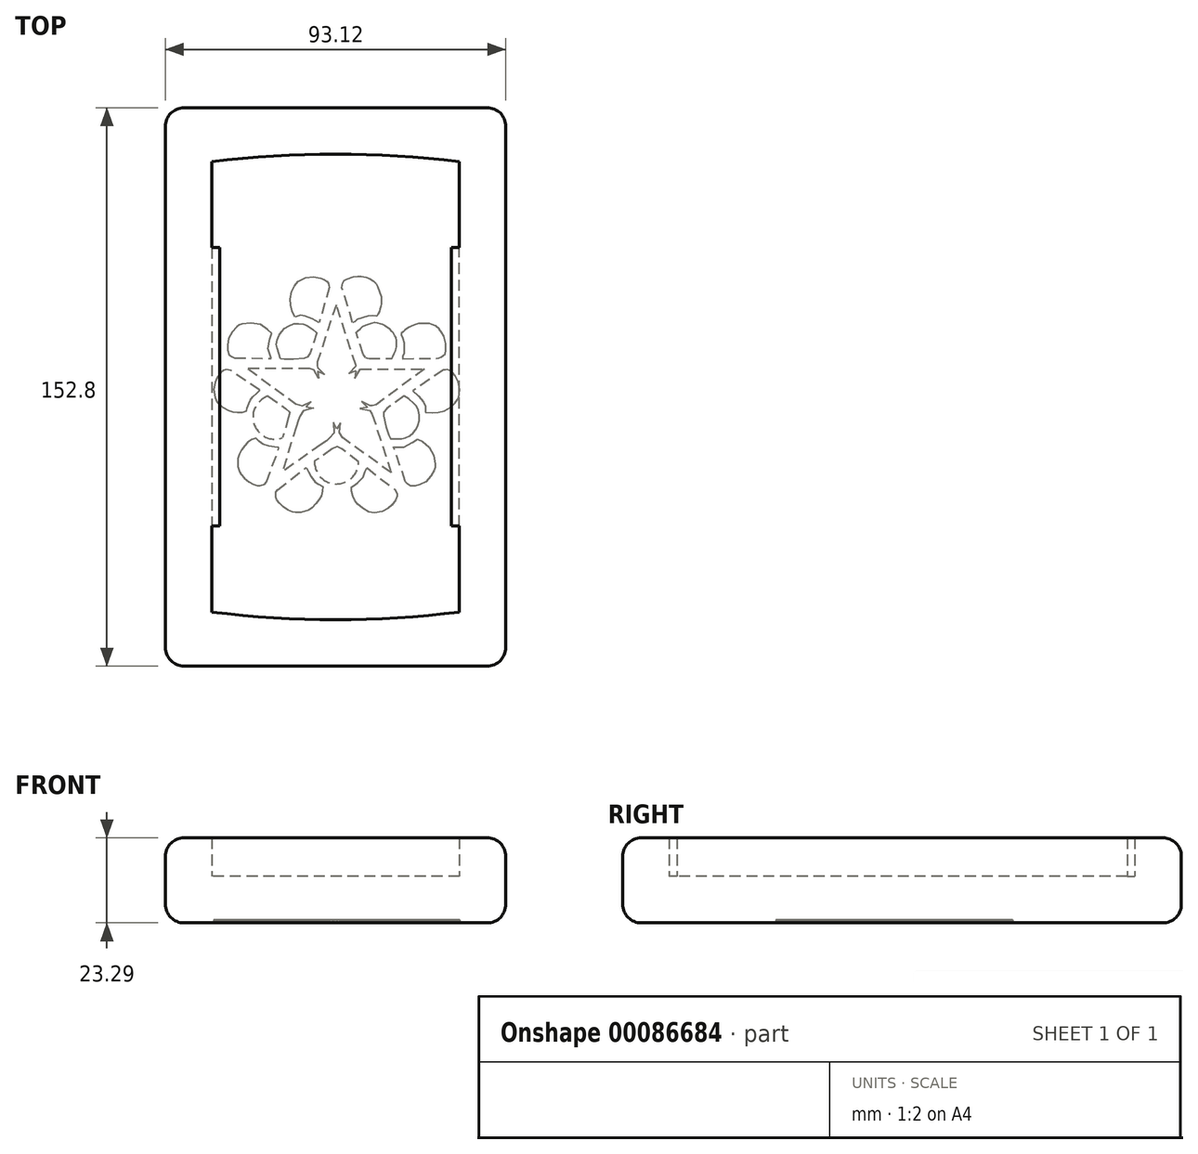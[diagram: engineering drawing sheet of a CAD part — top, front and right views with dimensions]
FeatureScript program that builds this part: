
annotation { "Feature Type Name" : "Feature", "Feature Type Description" : "" }
export const myFeature = defineFeature(function(context is Context, id is Id, definition is map)
    precondition{}
    {
        {
            var Q0;
            Q0=qCreatedBy(makeId("Top.planeOp"),FACE);
            var sketch = newSketch(context, id + "F0", { "sketchPlane" : qUnion([Q0])});
            skLineSegment(sketch, "E0.left", {"start": v(33.86, 61.62) * mm, "end": v(33.86, -61.62) * mm});
            skLineSegment(sketch, "E0.right", {"start": v(-33.86, 61.62) * mm, "end": v(-33.86, -61.62) * mm});
            skPoint(sketch, "E0.middle", {"position": v(0, 0) * mm});
            skLineSegment(sketch, "E1.bottom", {"start": v(0, 63.7) * mm, "end": v(0, 63.7) * mm});
            skLineSegment(sketch, "E1.top", {"start": v(0, -63.7) * mm, "end": v(0, -63.7) * mm});
            skArc(sketch, "E2", {"start": v(33.86, 61.62) * mm, "mid": v(0, 63.7) * mm, "end": v(-33.86, 61.62) * mm});
            skArc(sketch, "E3", {"start": v(-33.86, -61.62) * mm, "mid": v(0, -63.7) * mm, "end": v(33.86, -61.62) * mm});
            skLineSegment(sketch, "E4.bottom", {"start": v(46.56, 76.4) * mm, "end": v(-46.56, 76.4) * mm});
            skLineSegment(sketch, "E4.top", {"start": v(46.56, -76.4) * mm, "end": v(-46.56, -76.4) * mm});
            skLineSegment(sketch, "E4.left", {"start": v(46.56, 76.4) * mm, "end": v(46.56, -76.4) * mm});
            skLineSegment(sketch, "E4.right", {"start": v(-46.56, 76.4) * mm, "end": v(-46.56, -76.4) * mm});
            skSolve(sketch);
        }
        {
            var Q0;
            Q0=makeQuery(id+"F0.imprint","IMPRINT",FACE,{"disambiguationData":[TD([[makeQuery(id+"F0.imprint","IMPRINT",EDGE,{"derivedFrom":sQuery(id+"F0.wireOp",EDGE,"E0.left")}),-1.0]])]});
            extrude(context, id + "F1", {"entities" : qUnion([Q0]), "depth" : 12.7 * mm});
        }
        {
            var Q0;
            Q0=makeQuery(id+"F0.imprint","IMPRINT",FACE,{"disambiguationData":[TD([[makeQuery(id+"F0.imprint","IMPRINT",EDGE,{"derivedFrom":sQuery(id+"F0.wireOp",EDGE,"E0.left")}),1.0]])]});
            extrude(context, id + "F2", {"entities" : qUnion([Q0]), "operationType" : NewBodyOperationType.ADD, "depth" : 23.3 * mm});
        }
        {
            var Q0;
            Q0=makeQuery(id+"F2.opExtrude","SWEPT_FACE",FACE,{"disambiguationData":[OSD([sQuery(id+"F0.wireOp",EDGE,"E4.bottom")])]});
            var Q1;
            Q1=makeQuery(id+"F2.opExtrude","SWEPT_FACE",FACE,{"disambiguationData":[OSD([sQuery(id+"F0.wireOp",EDGE,"E4.left")])]});
            var Q2;
            Q2=makeQuery(id+"F2.opExtrude","SWEPT_FACE",FACE,{"disambiguationData":[OSD([sQuery(id+"F0.wireOp",EDGE,"E4.right")])]});
            var Q3;
            {var subQ0=sQuery(id+"F0.wireOp",EDGE,"E3");var subQ1=sQuery(id+"F0.wireOp",EDGE,"E2");var subQ2=sQuery(id+"F0.wireOp",EDGE,"E0.right");var subQ3=sQuery(id+"F0.wireOp",EDGE,"E0.left");Q3=makeQuery(id+"F2.boolean.opBoolean","MERGE",FACE,{"derivedFrom":[makeQuery(id+"F1.opExtrude","CAP_FACE",FACE,{"disambiguationData":[OSD([subQ3,subQ2,subQ1,subQ0])],"isStart":true}),makeQuery(id+"F2.opExtrude","CAP_FACE",FACE,{"disambiguationData":[OSD([subQ3,subQ2,subQ1,subQ0,sQuery(id+"F0.wireOp",EDGE,"E4.bottom"),sQuery(id+"F0.wireOp",EDGE,"E4.top"),sQuery(id+"F0.wireOp",EDGE,"E4.left"),sQuery(id+"F0.wireOp",EDGE,"E4.right")])],"isStart":true})]});}
            var Q4;
            Q4=makeQuery(id+"F2.opExtrude","SWEPT_FACE",FACE,{"disambiguationData":[OSD([sQuery(id+"F0.wireOp",EDGE,"E4.top")])]});
            fillet(context, id + "F3", {"entities" : qUnion([Q0, Q1, Q2, Q3, Q4]), "radius" : 5.08 * mm, "tangentPropagation" : true, "allowEdgeOverflow" : false});
        }
        {
            var Q0;
            Q0=makeQuery(id+"F2.opExtrude","SWEPT_FACE",FACE,{"disambiguationData":[OSD([sQuery(id+"F0.wireOp",EDGE,"E0.right")])]});
            var sketch = newSketch(context, id + "F4", { "sketchPlane" : qUnion([Q0])});
            skLineSegment(sketch, "E5.bottom", {"start": v(38.13, 23.3) * mm, "end": v(-38.07, 23.3) * mm});
            skLineSegment(sketch, "E5.top", {"start": v(38.13, 23.24) * mm, "end": v(-38.07, 23.24) * mm});
            skLineSegment(sketch, "E5.left", {"start": v(38.13, 23.3) * mm, "end": v(38.13, 23.24) * mm});
            skLineSegment(sketch, "E5.right", {"start": v(-38.07, 23.3) * mm, "end": v(-38.07, 23.24) * mm});
            skPoint(sketch, "E5.middle", {"position": v(0.03, 23.27) * mm});
            skSolve(sketch);
        }
        {
            var Q0;
            Q0=qSketchRegion(id+"F4",true);
            extrude(context, id + "F5", {"entities" : qUnion([Q0]), "operationType" : NewBodyOperationType.ADD, "depth" : 2.16 * mm});
        }
        {
            var Q0;
            Q0=makeQuery(id+"F2.opExtrude","SWEPT_FACE",FACE,{"disambiguationData":[OSD([sQuery(id+"F0.wireOp",EDGE,"E0.left")])]});
            var sketch = newSketch(context, id + "F6", { "sketchPlane" : qUnion([Q0])});
            skLineSegment(sketch, "E6.bottom", {"start": v(38.1, 23.3) * mm, "end": v(-38.1, 23.3) * mm});
            skLineSegment(sketch, "E6.top", {"start": v(38.1, 23.24) * mm, "end": v(-38.1, 23.24) * mm});
            skLineSegment(sketch, "E6.left", {"start": v(38.1, 23.3) * mm, "end": v(38.1, 23.24) * mm});
            skLineSegment(sketch, "E6.right", {"start": v(-38.1, 23.3) * mm, "end": v(-38.1, 23.24) * mm});
            skPoint(sketch, "E6.middle", {"position": v(0, 23.27) * mm});
            skSolve(sketch);
        }
        {
            var Q0;
            Q0=qSketchRegion(id+"F6",true);
            extrude(context, id + "F7", {"entities" : qUnion([Q0]), "operationType" : NewBodyOperationType.ADD, "depth" : 2.16 * mm});
        }
        {
            var Q0;
            {var subQ0=sQuery(id+"F0.wireOp",EDGE,"E3");var subQ1=sQuery(id+"F0.wireOp",EDGE,"E2");var subQ2=sQuery(id+"F0.wireOp",EDGE,"E0.right");var subQ3=sQuery(id+"F0.wireOp",EDGE,"E0.left");Q0=makeQuery(id+"F2.boolean.opBoolean","MERGE",FACE,{"derivedFrom":[makeQuery(id+"F1.opExtrude","CAP_FACE",FACE,{"disambiguationData":[OSD([subQ3,subQ2,subQ1,subQ0])],"isStart":true}),makeQuery(id+"F2.opExtrude","CAP_FACE",FACE,{"disambiguationData":[OSD([subQ3,subQ2,subQ1,subQ0,sQuery(id+"F0.wireOp",EDGE,"E4.bottom"),sQuery(id+"F0.wireOp",EDGE,"E4.top"),sQuery(id+"F0.wireOp",EDGE,"E4.left"),sQuery(id+"F0.wireOp",EDGE,"E4.right")])],"isStart":true})]});}
            var sketch = newSketch(context, id + "F8", { "sketchPlane" : qUnion([Q0])});
            skLineSegment(sketch, "E7", {"start": v(-21.27, 32.47) * mm, "end": v(-19.6, 31.78) * mm});
            skLineSegment(sketch, "E8", {"start": v(-19.6, 31.78) * mm, "end": v(-18.58, 31.78) * mm});
            skLineSegment(sketch, "E9", {"start": v(-18.58, 31.78) * mm, "end": v(-17.8, 32.76) * mm});
            skLineSegment(sketch, "E10", {"start": v(-17.8, 32.76) * mm, "end": v(-16.99, 33.84) * mm});
            skLineSegment(sketch, "E11", {"start": v(-16.99, 33.84) * mm, "end": v(-16.21, 34.55) * mm});
            skLineSegment(sketch, "E12", {"start": v(-16.21, 34.55) * mm, "end": v(-15.34, 35.36) * mm});
            skLineSegment(sketch, "E13", {"start": v(-15.34, 35.36) * mm, "end": v(-14.11, 36.07) * mm});
            skLineSegment(sketch, "E14", {"start": v(-14.11, 36.07) * mm, "end": v(-12.56, 36.76) * mm});
            skLineSegment(sketch, "E15", {"start": v(-12.56, 36.76) * mm, "end": v(-11.36, 37.15) * mm});
            skLineSegment(sketch, "E16", {"start": v(-11.36, 37.15) * mm, "end": v(-9.48, 37.15) * mm});
            skLineSegment(sketch, "E17", {"start": v(-9.48, 37.15) * mm, "end": v(-8.4, 36.84) * mm});
            skLineSegment(sketch, "E18", {"start": v(-8.4, 36.84) * mm, "end": v(-7.27, 36.3) * mm});
            skLineSegment(sketch, "E19", {"start": v(-7.27, 36.3) * mm, "end": v(-6.34, 35.7) * mm});
            skLineSegment(sketch, "E20", {"start": v(-6.34, 35.7) * mm, "end": v(-4.82, 34.45) * mm});
            skLineSegment(sketch, "E21", {"start": v(-4.82, 34.45) * mm, "end": v(-3.62, 32.98) * mm});
            skLineSegment(sketch, "E22", {"start": v(-3.62, 32.98) * mm, "end": v(-2.88, 31.54) * mm});
            skLineSegment(sketch, "E23", {"start": v(-2.88, 31.54) * mm, "end": v(-2.28, 29.72) * mm});
            skLineSegment(sketch, "E24", {"start": v(-2.28, 29.72) * mm, "end": v(-2.28, 27.54) * mm});
            skLineSegment(sketch, "E25", {"start": v(-2.28, 27.54) * mm, "end": v(2.77, 27.54) * mm});
            skLineSegment(sketch, "E26", {"start": v(2.77, 27.54) * mm, "end": v(2.77, 29.5) * mm});
            skLineSegment(sketch, "E27", {"start": v(2.77, 29.5) * mm, "end": v(2.88, 29.93) * mm});
            skLineSegment(sketch, "E28", {"start": v(2.88, 29.93) * mm, "end": v(3.16, 30.76) * mm});
            skLineSegment(sketch, "E29", {"start": v(3.16, 30.76) * mm, "end": v(3.54, 31.68) * mm});
            skLineSegment(sketch, "E30", {"start": v(3.54, 31.68) * mm, "end": v(3.9, 32.4) * mm});
            skLineSegment(sketch, "E31", {"start": v(3.9, 32.4) * mm, "end": v(4.44, 33.35) * mm});
            skLineSegment(sketch, "E32", {"start": v(4.44, 33.35) * mm, "end": v(5.66, 34.63) * mm});
            skLineSegment(sketch, "E33", {"start": v(5.66, 34.63) * mm, "end": v(7.02, 35.77) * mm});
            skLineSegment(sketch, "E34", {"start": v(7.02, 35.77) * mm, "end": v(8.66, 36.66) * mm});
            skLineSegment(sketch, "E35", {"start": v(8.66, 36.66) * mm, "end": v(10.1, 37.1) * mm});
            skLineSegment(sketch, "E36", {"start": v(10.1, 37.1) * mm, "end": v(11.8, 37.1) * mm});
            skLineSegment(sketch, "E37", {"start": v(11.8, 37.1) * mm, "end": v(12.73, 36.86) * mm});
            skLineSegment(sketch, "E38", {"start": v(12.73, 36.86) * mm, "end": v(14.16, 36.29) * mm});
            skLineSegment(sketch, "E39", {"start": v(14.16, 36.29) * mm, "end": v(15.13, 35.65) * mm});
            skLineSegment(sketch, "E40", {"start": v(15.13, 35.65) * mm, "end": v(16.14, 34.96) * mm});
            skLineSegment(sketch, "E41", {"start": v(16.14, 34.96) * mm, "end": v(17.24, 33.94) * mm});
            skLineSegment(sketch, "E42", {"start": v(17.24, 33.94) * mm, "end": v(18.1, 32.91) * mm});
            skLineSegment(sketch, "E43", {"start": v(18.1, 32.91) * mm, "end": v(18.87, 31.85) * mm});
            skLineSegment(sketch, "E44", {"start": v(18.87, 31.85) * mm, "end": v(19.38, 31.75) * mm});
            skLineSegment(sketch, "E45", {"start": v(19.38, 31.75) * mm, "end": v(19.9, 31.75) * mm});
            skLineSegment(sketch, "E46", {"start": v(19.9, 31.75) * mm, "end": v(20.48, 32.02) * mm});
            skLineSegment(sketch, "E47", {"start": v(20.48, 32.02) * mm, "end": v(21.15, 32.36) * mm});
            skLineSegment(sketch, "E48", {"start": v(21.15, 32.36) * mm, "end": v(21.48, 32.58) * mm});
            skLineSegment(sketch, "E49", {"start": v(21.48, 32.58) * mm, "end": v(21.48, 30.67) * mm});
            skLineSegment(sketch, "E50", {"start": v(21.48, 30.67) * mm, "end": v(21.48, 30.13) * mm});
            skLineSegment(sketch, "E51", {"start": v(21.48, 30.13) * mm, "end": v(21.75, 29.84) * mm});
            skLineSegment(sketch, "E52", {"start": v(21.75, 29.84) * mm, "end": v(21.91, 29.68) * mm});
            skLineSegment(sketch, "E53", {"start": v(21.91, 29.68) * mm, "end": v(22.88, 29.46) * mm});
            skLineSegment(sketch, "E54", {"start": v(22.88, 29.46) * mm, "end": v(24.3, 28.9) * mm});
            skLineSegment(sketch, "E55", {"start": v(24.3, 28.9) * mm, "end": v(25.68, 28.18) * mm});
            skLineSegment(sketch, "E56", {"start": v(25.68, 28.18) * mm, "end": v(26.6, 27.51) * mm});
            skLineSegment(sketch, "E57", {"start": v(26.6, 27.51) * mm, "end": v(27.55, 26.7) * mm});
            skLineSegment(sketch, "E58", {"start": v(27.55, 26.7) * mm, "end": v(28.24, 25.94) * mm});
            skLineSegment(sketch, "E59", {"start": v(28.24, 25.94) * mm, "end": v(28.75, 25.15) * mm});
            skLineSegment(sketch, "E60", {"start": v(28.75, 25.15) * mm, "end": v(29.25, 24.25) * mm});
            skLineSegment(sketch, "E61", {"start": v(29.25, 24.25) * mm, "end": v(29.62, 22.94) * mm});
            skLineSegment(sketch, "E62", {"start": v(29.62, 22.94) * mm, "end": v(29.62, 21.2) * mm});
            skLineSegment(sketch, "E63", {"start": v(29.62, 21.2) * mm, "end": v(29.47, 19.95) * mm});
            skLineSegment(sketch, "E64", {"start": v(29.47, 19.95) * mm, "end": v(29.11, 18.99) * mm});
            skLineSegment(sketch, "E65", {"start": v(29.11, 18.99) * mm, "end": v(28.56, 17.78) * mm});
            skLineSegment(sketch, "E66", {"start": v(28.56, 17.78) * mm, "end": v(27.74, 16.5) * mm});
            skLineSegment(sketch, "E67", {"start": v(27.74, 16.5) * mm, "end": v(27.09, 15.68) * mm});
            skLineSegment(sketch, "E68", {"start": v(27.09, 15.68) * mm, "end": v(26.37, 15.01) * mm});
            skLineSegment(sketch, "E69", {"start": v(26.37, 15.01) * mm, "end": v(25.39, 14.3) * mm});
            skLineSegment(sketch, "E70", {"start": v(25.39, 14.3) * mm, "end": v(24.12, 13.62) * mm});
            skLineSegment(sketch, "E71", {"start": v(24.12, 13.62) * mm, "end": v(23.25, 13.32) * mm});
            skLineSegment(sketch, "E72", {"start": v(23.25, 13.32) * mm, "end": v(22.98, 13.32) * mm});
            skLineSegment(sketch, "E73", {"start": v(22.98, 13.32) * mm, "end": v(22.98, 12.9) * mm});
            skLineSegment(sketch, "E74", {"start": v(22.98, 12.9) * mm, "end": v(23.57, 11.63) * mm});
            skLineSegment(sketch, "E75", {"start": v(23.57, 11.63) * mm, "end": v(24.07, 9.99) * mm});
            skLineSegment(sketch, "E76", {"start": v(24.07, 9.99) * mm, "end": v(24.55, 8.24) * mm});
            skLineSegment(sketch, "E77", {"start": v(24.55, 8.24) * mm, "end": v(25.04, 8.37) * mm});
            skLineSegment(sketch, "E78", {"start": v(25.04, 8.37) * mm, "end": v(26.4, 8.69) * mm});
            skLineSegment(sketch, "E79", {"start": v(26.4, 8.69) * mm, "end": v(27.63, 8.69) * mm});
            skLineSegment(sketch, "E80", {"start": v(27.63, 8.69) * mm, "end": v(28.99, 8.69) * mm});
            skLineSegment(sketch, "E81", {"start": v(28.99, 8.69) * mm, "end": v(30.34, 8.43) * mm});
            skLineSegment(sketch, "E82", {"start": v(30.34, 8.43) * mm, "end": v(31.78, 7.84) * mm});
            skLineSegment(sketch, "E83", {"start": v(31.78, 7.84) * mm, "end": v(33.1, 7.17) * mm});
            skLineSegment(sketch, "E84", {"start": v(33.1, 7.17) * mm, "end": v(34.13, 6.34) * mm});
            skLineSegment(sketch, "E85", {"start": v(34.13, 6.34) * mm, "end": v(35, 5.42) * mm});
            skLineSegment(sketch, "E86", {"start": v(35, 5.42) * mm, "end": v(35.78, 4.35) * mm});
            skLineSegment(sketch, "E87", {"start": v(35.78, 4.35) * mm, "end": v(36.28, 3.1) * mm});
            skLineSegment(sketch, "E88", {"start": v(36.28, 3.1) * mm, "end": v(36.41, 2.52) * mm});
            skLineSegment(sketch, "E89", {"start": v(36.41, 2.52) * mm, "end": v(36.41, 0.78) * mm});
            skLineSegment(sketch, "E90", {"start": v(36.41, 0.78) * mm, "end": v(36.41, -0.54) * mm});
            skLineSegment(sketch, "E91", {"start": v(36.41, -0.54) * mm, "end": v(35.56, -2.8) * mm});
            skLineSegment(sketch, "E92", {"start": v(35.56, -2.8) * mm, "end": v(35.05, -3.72) * mm});
            skLineSegment(sketch, "E93", {"start": v(35.05, -3.72) * mm, "end": v(34.58, -4.42) * mm});
            skLineSegment(sketch, "E94", {"start": v(34.58, -4.42) * mm, "end": v(33.74, -5.62) * mm});
            skLineSegment(sketch, "E95", {"start": v(33.74, -5.62) * mm, "end": v(33.74, -6.53) * mm});
            skLineSegment(sketch, "E96", {"start": v(33.74, -6.53) * mm, "end": v(34.2, -7.05) * mm});
            skLineSegment(sketch, "E97", {"start": v(34.2, -7.05) * mm, "end": v(35.23, -8.06) * mm});
            skLineSegment(sketch, "E98", {"start": v(35.23, -8.06) * mm, "end": v(34.19, -8.26) * mm});
            skLineSegment(sketch, "E99", {"start": v(34.19, -8.26) * mm, "end": v(33.47, -8.46) * mm});
            skLineSegment(sketch, "E100", {"start": v(33.47, -8.46) * mm, "end": v(32.65, -9.1) * mm});
            skLineSegment(sketch, "E101", {"start": v(32.65, -9.1) * mm, "end": v(32.65, -11.82) * mm});
            skLineSegment(sketch, "E102", {"start": v(32.65, -11.82) * mm, "end": v(32.24, -13.93) * mm});
            skLineSegment(sketch, "E103", {"start": v(32.24, -13.93) * mm, "end": v(31.52, -15.69) * mm});
            skLineSegment(sketch, "E104", {"start": v(31.52, -15.69) * mm, "end": v(30.52, -17.17) * mm});
            skLineSegment(sketch, "E105", {"start": v(30.52, -17.17) * mm, "end": v(29.45, -18.31) * mm});
            skLineSegment(sketch, "E106", {"start": v(29.45, -18.31) * mm, "end": v(27.46, -19.28) * mm});
            skLineSegment(sketch, "E107", {"start": v(27.46, -19.28) * mm, "end": v(25.53, -19.59) * mm});
            skLineSegment(sketch, "E108", {"start": v(25.53, -19.59) * mm, "end": v(24.13, -19.59) * mm});
            skLineSegment(sketch, "E109", {"start": v(24.13, -19.59) * mm, "end": v(23.04, -19.38) * mm});
            skLineSegment(sketch, "E110", {"start": v(23.04, -19.38) * mm, "end": v(21.7, -19.04) * mm});
            skLineSegment(sketch, "E111", {"start": v(21.7, -19.04) * mm, "end": v(20.63, -18.54) * mm});
            skLineSegment(sketch, "E112", {"start": v(20.63, -18.54) * mm, "end": v(19.62, -18.02) * mm});
            skLineSegment(sketch, "E113", {"start": v(19.62, -18.02) * mm, "end": v(18.92, -17.41) * mm});
            skLineSegment(sketch, "E114", {"start": v(18.92, -17.41) * mm, "end": v(18.3, -16.85) * mm});
            skLineSegment(sketch, "E115", {"start": v(18.3, -16.85) * mm, "end": v(17.6, -16.01) * mm});
            skLineSegment(sketch, "E116", {"start": v(17.6, -16.01) * mm, "end": v(17.18, -15.46) * mm});
            skLineSegment(sketch, "E117", {"start": v(17.18, -15.46) * mm, "end": v(14.88, -17.16) * mm});
            skLineSegment(sketch, "E118.MirrorCS", {"start": v(-11.14, -31.34) * mm, "end": v(-10.64, -31.65) * mm});
            skLineSegment(sketch, "E119.MirrorCS", {"start": v(-16.35, -15.66) * mm, "end": v(-15.33, -16.61) * mm});
            skLineSegment(sketch, "E120.MirrorCS", {"start": v(-34.29, -7.9) * mm, "end": v(-34.6, -8.14) * mm});
            skLineSegment(sketch, "E121.MirrorCS", {"start": v(-10.64, -31.65) * mm, "end": v(-8.98, -32.19) * mm});
            skLineSegment(sketch, "E122.MirrorCS", {"start": v(-12.2, -30.48) * mm, "end": v(-11.14, -31.34) * mm});
            skLineSegment(sketch, "E123.MirrorCS", {"start": v(-17.4, -16.52) * mm, "end": v(-16.84, -15.79) * mm});
            skLineSegment(sketch, "E124.MirrorCS", {"start": v(-18.42, -17.52) * mm, "end": v(-17.4, -16.52) * mm});
            skLineSegment(sketch, "E125.MirrorCS", {"start": v(-33.17, -6.4) * mm, "end": v(-33.33, -6.9) * mm});
            skLineSegment(sketch, "E126.MirrorCS", {"start": v(-33.88, -4.83) * mm, "end": v(-33.1, -5.88) * mm});
            skLineSegment(sketch, "E127.MirrorCS", {"start": v(-34.58, -3.69) * mm, "end": v(-33.88, -4.83) * mm});
            skLineSegment(sketch, "E128.MirrorCS", {"start": v(-33.33, -6.9) * mm, "end": v(-33.76, -7.36) * mm});
            skLineSegment(sketch, "E129.MirrorCS", {"start": v(-32.28, -8.9) * mm, "end": v(-32.08, -9.24) * mm});
            skLineSegment(sketch, "E130.MirrorCS", {"start": v(-33.76, -7.36) * mm, "end": v(-34.29, -7.9) * mm});
            skLineSegment(sketch, "E131.MirrorCS", {"start": v(-34.6, -8.14) * mm, "end": v(-32.78, -8.74) * mm});
            skLineSegment(sketch, "E132.MirrorCS", {"start": v(-33.1, -5.88) * mm, "end": v(-33.17, -6.4) * mm});
            skLineSegment(sketch, "E133.MirrorCS", {"start": v(-25.88, 8.7) * mm, "end": v(-26.33, 8.73) * mm});
            skLineSegment(sketch, "E134.MirrorCS", {"start": v(-28.78, 24.5) * mm, "end": v(-29.36, 22.71) * mm});
            skLineSegment(sketch, "E135.MirrorCS", {"start": v(-29.36, 22.71) * mm, "end": v(-29.4, 21.6) * mm});
            skLineSegment(sketch, "E136.MirrorCS", {"start": v(-29.4, 21.6) * mm, "end": v(-29.24, 20.35) * mm});
            skLineSegment(sketch, "E137.MirrorCS", {"start": v(-31.98, -9.45) * mm, "end": v(-32.07, -10.43) * mm});
            skLineSegment(sketch, "E138.MirrorCS", {"start": v(-35.9, 2.46) * mm, "end": v(-35.97, 1.5) * mm});
            skLineSegment(sketch, "E139.MirrorCS", {"start": v(0.7, -32.25) * mm, "end": v(1.57, -31.67) * mm});
            skLineSegment(sketch, "E140.MirrorCS", {"start": v(-35.37, 4.09) * mm, "end": v(-35.9, 2.46) * mm});
            skLineSegment(sketch, "E141.MirrorCS", {"start": v(-35.97, 1.5) * mm, "end": v(-35.86, -0.03) * mm});
            skLineSegment(sketch, "E142.MirrorCS", {"start": v(-28.2, 8.64) * mm, "end": v(-29, 8.52) * mm});
            skLineSegment(sketch, "E143.MirrorCS", {"start": v(-12.68, -19.02) * mm, "end": v(-13.4, -20.21) * mm});
            skLineSegment(sketch, "E144.MirrorCS", {"start": v(-3.48, -32.05) * mm, "end": v(-2.08, -31.63) * mm});
            skLineSegment(sketch, "E145.MirrorCS", {"start": v(-8.98, -32.19) * mm, "end": v(-7.73, -32.6) * mm});
            skLineSegment(sketch, "E146.MirrorCS", {"start": v(-24.01, 8.09) * mm, "end": v(-25.88, 8.7) * mm});
            skLineSegment(sketch, "E147.MirrorCS", {"start": v(-26.33, 8.73) * mm, "end": v(-27.2, 8.72) * mm});
            skLineSegment(sketch, "E148.MirrorCS", {"start": v(0.3, -32.87) * mm, "end": v(0.7, -32.25) * mm});
            skLineSegment(sketch, "E149.MirrorCS", {"start": v(-29.24, 20.35) * mm, "end": v(-28.96, 19.28) * mm});
            skLineSegment(sketch, "E150.MirrorCS", {"start": v(-0.22, -33.8) * mm, "end": v(0.3, -32.87) * mm});
            skLineSegment(sketch, "E151.MirrorCS", {"start": v(-13.4, -20.21) * mm, "end": v(-13.79, -21.39) * mm});
            skLineSegment(sketch, "E152.MirrorCS", {"start": v(-1.2, -31.91) * mm, "end": v(-0.86, -32.5) * mm});
            skLineSegment(sketch, "E153.MirrorCS", {"start": v(-13.79, -21.39) * mm, "end": v(-14.2, -22.68) * mm});
            skLineSegment(sketch, "E154.MirrorCS", {"start": v(-27.2, 8.72) * mm, "end": v(-28.2, 8.64) * mm});
            skLineSegment(sketch, "E155.MirrorCS", {"start": v(-4.3, -32.28) * mm, "end": v(-3.48, -32.05) * mm});
            skLineSegment(sketch, "E156.MirrorCS", {"start": v(-28.04, 25.52) * mm, "end": v(-28.78, 24.5) * mm});
            skLineSegment(sketch, "E157.MirrorCS", {"start": v(-2.08, -31.63) * mm, "end": v(-1.2, -31.91) * mm});
            skLineSegment(sketch, "E158.MirrorCS", {"start": v(-0.86, -32.5) * mm, "end": v(-0.22, -33.8) * mm});
            skLineSegment(sketch, "E159.MirrorCS", {"start": v(-15.33, -16.61) * mm, "end": v(-13.92, -17.6) * mm});
            skLineSegment(sketch, "E160.MirrorCS", {"start": v(-30.38, -16.63) * mm, "end": v(-29.8, -17.35) * mm});
            skLineSegment(sketch, "E161.MirrorCS", {"start": v(12.86, -29.88) * mm, "end": v(13.75, -28.15) * mm});
            skLineSegment(sketch, "E162.MirrorCS", {"start": v(14.18, -26.8) * mm, "end": v(14.32, -25.7) * mm});
            skLineSegment(sketch, "E163.MirrorCS", {"start": v(-32.07, -10.43) * mm, "end": v(-31.98, -11.95) * mm});
            skLineSegment(sketch, "E164.MirrorCS", {"start": v(-27.96, -18.86) * mm, "end": v(-26.3, -19.4) * mm});
            skLineSegment(sketch, "E165.MirrorCS", {"start": v(-30.89, -15.73) * mm, "end": v(-30.38, -16.63) * mm});
            skLineSegment(sketch, "E166.MirrorCS", {"start": v(-34.51, 5.31) * mm, "end": v(-35.37, 4.09) * mm});
            skLineSegment(sketch, "E167.MirrorCS", {"start": v(-29.09, -18.1) * mm, "end": v(-27.96, -18.86) * mm});
            skLineSegment(sketch, "E168.MirrorCS", {"start": v(-12.4, -18.6) * mm, "end": v(-12.68, -19.02) * mm});
            skLineSegment(sketch, "E169.MirrorCS", {"start": v(-13.92, -17.6) * mm, "end": v(-12.4, -18.6) * mm});
            skLineSegment(sketch, "E170.MirrorCS", {"start": v(13.75, -28.15) * mm, "end": v(14.18, -26.8) * mm});
            skLineSegment(sketch, "E171.MirrorCS", {"start": v(-29.8, -17.35) * mm, "end": v(-29.09, -18.1) * mm});
            skLineSegment(sketch, "E172.MirrorCS", {"start": v(-7.73, -32.6) * mm, "end": v(-5.33, -32.48) * mm});
            skLineSegment(sketch, "E173.MirrorCS", {"start": v(-20.27, -18.7) * mm, "end": v(-19.41, -18.23) * mm});
            skLineSegment(sketch, "E174.MirrorCS", {"start": v(-14.04, -27.05) * mm, "end": v(-13.57, -28.3) * mm});
            skLineSegment(sketch, "E175.MirrorCS", {"start": v(-28.24, 17.44) * mm, "end": v(-27.21, 15.85) * mm});
            skLineSegment(sketch, "E176.MirrorCS", {"start": v(12.8, -19.49) * mm, "end": v(12.4, -18.92) * mm});
            skLineSegment(sketch, "E177.MirrorCS", {"start": v(12.4, -18.92) * mm, "end": v(14.74, -17.26) * mm});
            skLineSegment(sketch, "E178.MirrorCS", {"start": v(-28.96, 19.28) * mm, "end": v(-28.24, 17.44) * mm});
            skLineSegment(sketch, "E179.MirrorCS", {"start": v(1.57, -31.67) * mm, "end": v(4.16, -32.51) * mm});
            skLineSegment(sketch, "E180.MirrorCS", {"start": v(-13.57, -28.3) * mm, "end": v(-12.96, -29.4) * mm});
            skLineSegment(sketch, "E181.MirrorCS", {"start": v(11.32, -31.47) * mm, "end": v(12.86, -29.88) * mm});
            skLineSegment(sketch, "E182.MirrorCS", {"start": v(-27.21, 15.85) * mm, "end": v(-26.08, 14.7) * mm});
            skLineSegment(sketch, "E183.MirrorCS", {"start": v(14.32, -25.7) * mm, "end": v(14.42, -24.32) * mm});
            skLineSegment(sketch, "E184.MirrorCS", {"start": v(-19.41, -18.23) * mm, "end": v(-18.42, -17.52) * mm});
            skLineSegment(sketch, "E185.MirrorCS", {"start": v(-21.27, 32.47) * mm, "end": v(-21.12, 30.67) * mm});
            skLineSegment(sketch, "E186.MirrorCS", {"start": v(-21.12, 30.67) * mm, "end": v(-21.44, 29.7) * mm});
            skLineSegment(sketch, "E187.MirrorCS", {"start": v(-21.44, 29.7) * mm, "end": v(-22.61, 29.26) * mm});
            skLineSegment(sketch, "E188.MirrorCS", {"start": v(-23.89, 28.83) * mm, "end": v(-24.8, 28.3) * mm});
            skLineSegment(sketch, "E189.MirrorCS", {"start": v(-22.61, 29.26) * mm, "end": v(-23.89, 28.83) * mm});
            skLineSegment(sketch, "E190.MirrorCS", {"start": v(-21.25, -19.07) * mm, "end": v(-20.27, -18.7) * mm});
            skLineSegment(sketch, "E191.MirrorCS", {"start": v(-25.85, 27.73) * mm, "end": v(-26.9, 26.79) * mm});
            skLineSegment(sketch, "E192.MirrorCS", {"start": v(-24.8, 28.3) * mm, "end": v(-25.85, 27.73) * mm});
            skLineSegment(sketch, "E193.MirrorCS", {"start": v(13.38, -20.43) * mm, "end": v(12.8, -19.49) * mm});
            skLineSegment(sketch, "E194.MirrorCS", {"start": v(-14.27, -25.6) * mm, "end": v(-14.04, -27.05) * mm});
            skLineSegment(sketch, "E195.MirrorCS", {"start": v(-30.06, 8.3) * mm, "end": v(-31.65, 7.54) * mm});
            skLineSegment(sketch, "E196.MirrorCS", {"start": v(-22.72, -19.45) * mm, "end": v(-21.25, -19.07) * mm});
            skLineSegment(sketch, "E197.MirrorCS", {"start": v(-31.98, -11.95) * mm, "end": v(-31.72, -13.5) * mm});
            skLineSegment(sketch, "E198.MirrorCS", {"start": v(-35.86, -0.03) * mm, "end": v(-35.56, -1.15) * mm});
            skLineSegment(sketch, "E199.MirrorCS", {"start": v(-14.38, -24.04) * mm, "end": v(-14.27, -25.6) * mm});
            skLineSegment(sketch, "E200.MirrorCS", {"start": v(-26.08, 14.7) * mm, "end": v(-24.53, 13.57) * mm});
            skLineSegment(sketch, "E201.MirrorCS", {"start": v(6.29, -32.77) * mm, "end": v(8.19, -32.63) * mm});
            skLineSegment(sketch, "E202.MirrorCS", {"start": v(9.9, -32.14) * mm, "end": v(11.32, -31.47) * mm});
            skLineSegment(sketch, "E203.MirrorCS", {"start": v(13.72, -21.18) * mm, "end": v(13.38, -20.43) * mm});
            skLineSegment(sketch, "E204.MirrorCS", {"start": v(-35.22, -2.32) * mm, "end": v(-34.58, -3.69) * mm});
            skLineSegment(sketch, "E205.MirrorCS", {"start": v(14.42, -24.32) * mm, "end": v(14.27, -23.16) * mm});
            skLineSegment(sketch, "E206.MirrorCS", {"start": v(-31.37, -14.58) * mm, "end": v(-30.89, -15.73) * mm});
            skLineSegment(sketch, "E207.MirrorCS", {"start": v(-33.16, 6.6) * mm, "end": v(-34.51, 5.31) * mm});
            skLineSegment(sketch, "E208.MirrorCS", {"start": v(14.27, -23.16) * mm, "end": v(14.09, -22.03) * mm});
            skLineSegment(sketch, "E209.MirrorCS", {"start": v(-26.3, -19.4) * mm, "end": v(-25.07, -19.65) * mm});
            skLineSegment(sketch, "E210.MirrorCS", {"start": v(-25.07, -19.65) * mm, "end": v(-24.04, -19.6) * mm});
            skLineSegment(sketch, "E211.MirrorCS", {"start": v(-12.96, -29.4) * mm, "end": v(-12.2, -30.48) * mm});
            skLineSegment(sketch, "E212.MirrorCS", {"start": v(-26.9, 26.79) * mm, "end": v(-28.04, 25.52) * mm});
            skLineSegment(sketch, "E213.MirrorCS", {"start": v(-35.56, -1.15) * mm, "end": v(-35.22, -2.32) * mm});
            skLineSegment(sketch, "E214.MirrorCS", {"start": v(-31.72, -13.5) * mm, "end": v(-31.37, -14.58) * mm});
            skLineSegment(sketch, "E215.MirrorCS", {"start": v(-31.65, 7.54) * mm, "end": v(-33.16, 6.6) * mm});
            skLineSegment(sketch, "E216.MirrorCS", {"start": v(-24.53, 13.57) * mm, "end": v(-22.45, 12.9) * mm});
            skLineSegment(sketch, "E217.MirrorCS", {"start": v(14.09, -22.03) * mm, "end": v(13.72, -21.18) * mm});
            skLineSegment(sketch, "E218.MirrorCS", {"start": v(4.16, -32.51) * mm, "end": v(6.29, -32.77) * mm});
            skLineSegment(sketch, "E219.MirrorCS", {"start": v(-5.33, -32.48) * mm, "end": v(-4.3, -32.28) * mm});
            skLineSegment(sketch, "E220.MirrorCS", {"start": v(-29, 8.52) * mm, "end": v(-30.06, 8.3) * mm});
            skLineSegment(sketch, "E221.MirrorCS", {"start": v(-24.04, -19.6) * mm, "end": v(-22.72, -19.45) * mm});
            skLineSegment(sketch, "E222.MirrorCS", {"start": v(8.19, -32.63) * mm, "end": v(9.9, -32.14) * mm});
            skLineSegment(sketch, "E223.MirrorCS", {"start": v(-14.2, -22.68) * mm, "end": v(-14.38, -24.04) * mm});
            skLineSegment(sketch, "E224.MirrorCS", {"start": v(-22.45, 12.9) * mm, "end": v(-24.01, 8.09) * mm});
            skLineSegment(sketch, "E225", {"start": v(15.85, 16.5) * mm, "end": v(17.4, 16.5) * mm});
            skLineSegment(sketch, "E226", {"start": v(17.4, 16.5) * mm, "end": v(18.7, 16.5) * mm});
            skLineSegment(sketch, "E227", {"start": v(18.7, 16.5) * mm, "end": v(21.06, 15.24) * mm});
            skLineSegment(sketch, "E228", {"start": v(21.06, 15.24) * mm, "end": v(22.35, 14.34) * mm});
            skLineSegment(sketch, "E229", {"start": v(22.35, 14.34) * mm, "end": v(23.73, 15) * mm});
            skLineSegment(sketch, "E230", {"start": v(23.73, 15) * mm, "end": v(25.54, 16.43) * mm});
            skLineSegment(sketch, "E231", {"start": v(25.54, 16.43) * mm, "end": v(26.77, 18.8) * mm});
            skLineSegment(sketch, "E232", {"start": v(26.77, 18.8) * mm, "end": v(27.27, 21.17) * mm});
            skLineSegment(sketch, "E233", {"start": v(27.27, 21.17) * mm, "end": v(27.27, 22.02) * mm});
            skLineSegment(sketch, "E234", {"start": v(27.27, 22.02) * mm, "end": v(26.97, 22.77) * mm});
            skLineSegment(sketch, "E235", {"start": v(26.97, 22.77) * mm, "end": v(26.1, 24.39) * mm});
            skLineSegment(sketch, "E236", {"start": v(26.1, 24.39) * mm, "end": v(24.66, 25.96) * mm});
            skLineSegment(sketch, "E237", {"start": v(24.66, 25.96) * mm, "end": v(23.06, 26.79) * mm});
            skLineSegment(sketch, "E238", {"start": v(23.06, 26.79) * mm, "end": v(21.81, 27.17) * mm});
            skLineSegment(sketch, "E239", {"start": v(21.81, 27.17) * mm, "end": v(20.44, 27.17) * mm});
            skLineSegment(sketch, "E240", {"start": v(20.44, 27.17) * mm, "end": v(19.67, 26.66) * mm});
            skLineSegment(sketch, "E241", {"start": v(19.67, 26.66) * mm, "end": v(19.13, 25.96) * mm});
            skLineSegment(sketch, "E242", {"start": v(19.13, 25.96) * mm, "end": v(15.85, 16.5) * mm});
            skLineSegment(sketch, "E243", {"start": v(15.02, 14.15) * mm, "end": v(18.02, 14.15) * mm});
            skLineSegment(sketch, "E244", {"start": v(18.02, 14.15) * mm, "end": v(19.06, 13.99) * mm});
            skLineSegment(sketch, "E245", {"start": v(19.06, 13.99) * mm, "end": v(20.18, 13.4) * mm});
            skLineSegment(sketch, "E246", {"start": v(20.18, 13.4) * mm, "end": v(21.25, 12.54) * mm});
            skLineSegment(sketch, "E247", {"start": v(21.25, 12.54) * mm, "end": v(21.97, 11.67) * mm});
            skLineSegment(sketch, "E248", {"start": v(21.97, 11.67) * mm, "end": v(22.54, 10.49) * mm});
            skLineSegment(sketch, "E249", {"start": v(22.54, 10.49) * mm, "end": v(22.88, 9.2) * mm});
            skLineSegment(sketch, "E250", {"start": v(22.88, 9.2) * mm, "end": v(22.96, 7.66) * mm});
            skLineSegment(sketch, "E251", {"start": v(22.96, 7.66) * mm, "end": v(22.68, 6.42) * mm});
            skLineSegment(sketch, "E252", {"start": v(22.68, 6.42) * mm, "end": v(22.11, 5.23) * mm});
            skLineSegment(sketch, "E253", {"start": v(22.11, 5.23) * mm, "end": v(21.4, 4.47) * mm});
            skLineSegment(sketch, "E254", {"start": v(21.4, 4.47) * mm, "end": v(20.03, 3.28) * mm});
            skLineSegment(sketch, "E255", {"start": v(20.03, 3.28) * mm, "end": v(18.7, 2.49) * mm});
            skLineSegment(sketch, "E256", {"start": v(18.7, 2.49) * mm, "end": v(14, 5.97) * mm});
            skLineSegment(sketch, "E257", {"start": v(14, 5.97) * mm, "end": v(13.11, 6.98) * mm});
            skLineSegment(sketch, "E258", {"start": v(13.11, 6.98) * mm, "end": v(13.11, 8) * mm});
            skLineSegment(sketch, "E259", {"start": v(13.11, 8) * mm, "end": v(13.73, 10.88) * mm});
            skLineSegment(sketch, "E260", {"start": v(13.73, 10.88) * mm, "end": v(14.56, 13.18) * mm});
            skLineSegment(sketch, "E261", {"start": v(14.56, 13.18) * mm, "end": v(15.02, 14.15) * mm});
            skLineSegment(sketch, "E262", {"start": v(21.12, 1.07) * mm, "end": v(22.66, 2.44) * mm});
            skLineSegment(sketch, "E263", {"start": v(22.66, 2.44) * mm, "end": v(24, 4.1) * mm});
            skLineSegment(sketch, "E264", {"start": v(24, 4.1) * mm, "end": v(24.6, 5.32) * mm});
            skLineSegment(sketch, "E265", {"start": v(24.6, 5.32) * mm, "end": v(24.6, 6.9) * mm});
            skLineSegment(sketch, "E266", {"start": v(24.6, 6.9) * mm, "end": v(26.49, 7.13) * mm});
            skLineSegment(sketch, "E267", {"start": v(26.49, 7.13) * mm, "end": v(28.07, 6.97) * mm});
            skLineSegment(sketch, "E268", {"start": v(28.07, 6.97) * mm, "end": v(29.7, 6.5) * mm});
            skLineSegment(sketch, "E269", {"start": v(29.7, 6.5) * mm, "end": v(31.59, 5.48) * mm});
            skLineSegment(sketch, "E270", {"start": v(31.59, 5.48) * mm, "end": v(32.75, 4.42) * mm});
            skLineSegment(sketch, "E271", {"start": v(32.75, 4.42) * mm, "end": v(33.67, 2.98) * mm});
            skLineSegment(sketch, "E272", {"start": v(33.67, 2.98) * mm, "end": v(33.96, 0.76) * mm});
            skLineSegment(sketch, "E273", {"start": v(33.96, 0.76) * mm, "end": v(33.57, -1.36) * mm});
            skLineSegment(sketch, "E274", {"start": v(33.57, -1.36) * mm, "end": v(32.63, -3.05) * mm});
            skLineSegment(sketch, "E275", {"start": v(32.63, -3.05) * mm, "end": v(31.94, -3.97) * mm});
            skLineSegment(sketch, "E276", {"start": v(31.94, -3.97) * mm, "end": v(31.2, -4.47) * mm});
            skLineSegment(sketch, "E277", {"start": v(31.2, -4.47) * mm, "end": v(30.57, -4.72) * mm});
            skLineSegment(sketch, "E278", {"start": v(30.57, -4.72) * mm, "end": v(29.99, -4.62) * mm});
            skLineSegment(sketch, "E279", {"start": v(29.99, -4.62) * mm, "end": v(29.49, -4.62) * mm});
            skLineSegment(sketch, "E280", {"start": v(29.49, -4.62) * mm, "end": v(21.12, 1.07) * mm});
            skLineSegment(sketch, "E281", {"start": v(8.18, -8.08) * mm, "end": v(8.58, -7.94) * mm});
            skLineSegment(sketch, "E282", {"start": v(8.58, -7.94) * mm, "end": v(9.16, -7.75) * mm});
            skLineSegment(sketch, "E283", {"start": v(9.16, -7.75) * mm, "end": v(15.4, -7.75) * mm});
            skLineSegment(sketch, "E284", {"start": v(15.4, -7.75) * mm, "end": v(15.73, -8.32) * mm});
            skLineSegment(sketch, "E285", {"start": v(15.73, -8.32) * mm, "end": v(16.08, -9.15) * mm});
            skLineSegment(sketch, "E286", {"start": v(16.08, -9.15) * mm, "end": v(16.4, -9.98) * mm});
            skLineSegment(sketch, "E287", {"start": v(16.4, -9.98) * mm, "end": v(16.62, -10.94) * mm});
            skLineSegment(sketch, "E288", {"start": v(16.62, -10.94) * mm, "end": v(16.62, -11.6) * mm});
            skLineSegment(sketch, "E289", {"start": v(16.62, -11.6) * mm, "end": v(16.62, -12.57) * mm});
            skLineSegment(sketch, "E290", {"start": v(16.62, -12.57) * mm, "end": v(16.5, -13.44) * mm});
            skLineSegment(sketch, "E291", {"start": v(16.5, -13.44) * mm, "end": v(16.23, -14) * mm});
            skLineSegment(sketch, "E292", {"start": v(16.23, -14) * mm, "end": v(15.76, -14.82) * mm});
            skLineSegment(sketch, "E293", {"start": v(15.76, -14.82) * mm, "end": v(15.38, -15.19) * mm});
            skLineSegment(sketch, "E294", {"start": v(15.38, -15.19) * mm, "end": v(14.77, -15.87) * mm});
            skLineSegment(sketch, "E295", {"start": v(14.77, -15.87) * mm, "end": v(14.15, -16.31) * mm});
            skLineSegment(sketch, "E296", {"start": v(18.32, -7.7) * mm, "end": v(28.26, -7.86) * mm});
            skLineSegment(sketch, "E297", {"start": v(28.26, -7.86) * mm, "end": v(28.89, -8.15) * mm});
            skLineSegment(sketch, "E298", {"start": v(28.89, -8.15) * mm, "end": v(29.4, -8.5) * mm});
            skLineSegment(sketch, "E299", {"start": v(29.4, -8.5) * mm, "end": v(29.98, -9.07) * mm});
            skLineSegment(sketch, "E300", {"start": v(29.98, -9.07) * mm, "end": v(30.13, -9.9) * mm});
            skLineSegment(sketch, "E301", {"start": v(30.13, -9.9) * mm, "end": v(30.13, -11.8) * mm});
            skLineSegment(sketch, "E302", {"start": v(30.13, -11.8) * mm, "end": v(29.94, -12.82) * mm});
            skLineSegment(sketch, "E303", {"start": v(29.94, -12.82) * mm, "end": v(29.6, -13.86) * mm});
            skLineSegment(sketch, "E304", {"start": v(29.6, -13.86) * mm, "end": v(29, -14.94) * mm});
            skLineSegment(sketch, "E305", {"start": v(29, -14.94) * mm, "end": v(28.38, -15.84) * mm});
            skLineSegment(sketch, "E306", {"start": v(28.38, -15.84) * mm, "end": v(27.33, -16.63) * mm});
            skLineSegment(sketch, "E307", {"start": v(27.33, -16.63) * mm, "end": v(26.38, -17.1) * mm});
            skLineSegment(sketch, "E308", {"start": v(26.38, -17.1) * mm, "end": v(25.63, -17.26) * mm});
            skLineSegment(sketch, "E309", {"start": v(25.63, -17.26) * mm, "end": v(22.63, -17.26) * mm});
            skLineSegment(sketch, "E310", {"start": v(22.63, -17.26) * mm, "end": v(21.9, -17.08) * mm});
            skLineSegment(sketch, "E311", {"start": v(21.9, -17.08) * mm, "end": v(20.81, -16.67) * mm});
            skLineSegment(sketch, "E312", {"start": v(20.81, -16.67) * mm, "end": v(20.1, -16.32) * mm});
            skLineSegment(sketch, "E313", {"start": v(20.1, -16.32) * mm, "end": v(19.47, -15.9) * mm});
            skLineSegment(sketch, "E314", {"start": v(19.47, -15.9) * mm, "end": v(18.93, -15.5) * mm});
            skLineSegment(sketch, "E315", {"start": v(18.93, -15.5) * mm, "end": v(18.4, -15.03) * mm});
            skLineSegment(sketch, "E316", {"start": v(18.4, -15.03) * mm, "end": v(17.98, -14.61) * mm});
            skLineSegment(sketch, "E317", {"start": v(17.98, -14.61) * mm, "end": v(17.98, -14.27) * mm});
            skLineSegment(sketch, "E318", {"start": v(17.98, -14.27) * mm, "end": v(18.38, -13.4) * mm});
            skLineSegment(sketch, "E319", {"start": v(18.38, -13.4) * mm, "end": v(18.73, -12.13) * mm});
            skLineSegment(sketch, "E320", {"start": v(18.73, -12.13) * mm, "end": v(18.73, -10.3) * mm});
            skLineSegment(sketch, "E321", {"start": v(18.73, -10.3) * mm, "end": v(18.73, -9.15) * mm});
            skLineSegment(sketch, "E322", {"start": v(18.73, -9.15) * mm, "end": v(18.38, -8.26) * mm});
            skLineSegment(sketch, "E323", {"start": v(18.38, -8.26) * mm, "end": v(18.32, -7.7) * mm});
            skLineSegment(sketch, "E324", {"start": v(5.5, -4.4) * mm, "end": v(5.3, -2.36) * mm});
            skLineSegment(sketch, "E325", {"start": v(5.3, -2.36) * mm, "end": v(6.82, -4.9) * mm});
            skLineSegment(sketch, "E326", {"start": v(6.82, -4.9) * mm, "end": v(24.32, -4.9) * mm});
            skLineSegment(sketch, "E327", {"start": v(24.32, -4.9) * mm, "end": v(11.08, 4.86) * mm});
            skLineSegment(sketch, "E328", {"start": v(11.08, 4.86) * mm, "end": v(10.05, 5.22) * mm});
            skLineSegment(sketch, "E329", {"start": v(10.05, 5.22) * mm, "end": v(9.5, 5.2) * mm});
            skLineSegment(sketch, "E330", {"start": v(9.5, 5.2) * mm, "end": v(7.19, 4.04) * mm});
            skLineSegment(sketch, "E331", {"start": v(7.19, 4.04) * mm, "end": v(8.63, 5.58) * mm});
            skLineSegment(sketch, "E332", {"start": v(8.63, 5.58) * mm, "end": v(8.43, 5.65) * mm});
            skLineSegment(sketch, "E333", {"start": v(8.43, 5.65) * mm, "end": v(6.65, 5.95) * mm});
            skLineSegment(sketch, "E334", {"start": v(6.65, 5.95) * mm, "end": v(9.32, 6.44) * mm});
            skLineSegment(sketch, "E335", {"start": v(9.32, 6.44) * mm, "end": v(9.99, 7.43) * mm});
            skLineSegment(sketch, "E336", {"start": v(9.99, 7.43) * mm, "end": v(15.17, 23.5) * mm});
            skLineSegment(sketch, "E337", {"start": v(15.17, 23.5) * mm, "end": v(2, 13.98) * mm});
            skLineSegment(sketch, "E338", {"start": v(2, 13.98) * mm, "end": v(1, 12.48) * mm});
            skLineSegment(sketch, "E339", {"start": v(1, 12.48) * mm, "end": v(1.3, 9.82) * mm});
            skLineSegment(sketch, "E340", {"start": v(1.3, 9.82) * mm, "end": v(0.32, 11.54) * mm});
            skLineSegment(sketch, "E341", {"start": v(0.32, 11.54) * mm, "end": v(-0.6, 9.8) * mm});
            skLineSegment(sketch, "E342", {"start": v(-0.6, 9.8) * mm, "end": v(-0.42, 12.64) * mm});
            skLineSegment(sketch, "E343", {"start": v(-0.42, 12.64) * mm, "end": v(-1.55, 13.9) * mm});
            skLineSegment(sketch, "E344", {"start": v(-1.55, 13.9) * mm, "end": v(-2.53, 14.77) * mm});
            skLineSegment(sketch, "E345", {"start": v(-2.53, 14.77) * mm, "end": v(-3.95, 15.74) * mm});
            skLineSegment(sketch, "E346", {"start": v(-3.95, 15.74) * mm, "end": v(-14.62, 23.32) * mm});
            skLineSegment(sketch, "E347", {"start": v(6.32, 20.53) * mm, "end": v(1.65, 16.96) * mm});
            skLineSegment(sketch, "E348", {"start": v(1.65, 16.96) * mm, "end": v(0.37, 16.3) * mm});
            skLineSegment(sketch, "E349", {"start": v(0.37, 16.3) * mm, "end": v(-0.92, 17) * mm});
            skLineSegment(sketch, "E350", {"start": v(-0.92, 17) * mm, "end": v(-5.77, 20.34) * mm});
            skArc(sketch, "E351", {"start": v(6.32, 20.53) * mm, "mid": v(0.18, 26.57) * mm, "end": v(-5.77, 20.34) * mm});
            skLineSegment(sketch, "E352", {"start": v(8.66, 22.22) * mm, "end": v(16.14, 28.07) * mm});
            skLineSegment(sketch, "E353", {"start": v(16.14, 28.07) * mm, "end": v(16.83, 29.18) * mm});
            skLineSegment(sketch, "E354", {"start": v(16.83, 29.18) * mm, "end": v(16.82, 29.99) * mm});
            skLineSegment(sketch, "E355", {"start": v(16.82, 29.99) * mm, "end": v(16.47, 30.88) * mm});
            skLineSegment(sketch, "E356", {"start": v(16.47, 30.88) * mm, "end": v(15.41, 32.3) * mm});
            skLineSegment(sketch, "E357", {"start": v(15.41, 32.3) * mm, "end": v(14.38, 33.2) * mm});
            skLineSegment(sketch, "E358", {"start": v(14.38, 33.2) * mm, "end": v(12.72, 34.17) * mm});
            skLineSegment(sketch, "E359", {"start": v(12.72, 34.17) * mm, "end": v(10.53, 34.47) * mm});
            skLineSegment(sketch, "E360", {"start": v(10.53, 34.47) * mm, "end": v(9.11, 34.3) * mm});
            skLineSegment(sketch, "E361", {"start": v(9.11, 34.3) * mm, "end": v(7.36, 33.29) * mm});
            skLineSegment(sketch, "E362", {"start": v(7.36, 33.29) * mm, "end": v(6, 32.04) * mm});
            skLineSegment(sketch, "E363", {"start": v(6, 32.04) * mm, "end": v(5.27, 31.08) * mm});
            skLineSegment(sketch, "E364", {"start": v(5.27, 31.08) * mm, "end": v(4.78, 29.91) * mm});
            skLineSegment(sketch, "E365", {"start": v(4.78, 29.91) * mm, "end": v(4.31, 28.55) * mm});
            skLineSegment(sketch, "E366", {"start": v(4.31, 28.55) * mm, "end": v(4.31, 27.34) * mm});
            skLineSegment(sketch, "E367", {"start": v(4.31, 27.34) * mm, "end": v(5.04, 26.96) * mm});
            skLineSegment(sketch, "E368", {"start": v(5.04, 26.96) * mm, "end": v(6.03, 26.2) * mm});
            skLineSegment(sketch, "E369", {"start": v(6.03, 26.2) * mm, "end": v(6.74, 25.49) * mm});
            skLineSegment(sketch, "E370", {"start": v(6.74, 25.49) * mm, "end": v(7.5, 24.67) * mm});
            skLineSegment(sketch, "E371", {"start": v(7.5, 24.67) * mm, "end": v(8.1, 23.22) * mm});
            skLineSegment(sketch, "E372", {"start": v(8.1, 23.22) * mm, "end": v(8.54, 22.22) * mm});
            skLineSegment(sketch, "E373", {"start": v(8.54, 22.22) * mm, "end": v(8.66, 22.22) * mm});
            skLineSegment(sketch, "E374", {"start": v(-7.97, 22.23) * mm, "end": v(-7.48, 23.25) * mm});
            skLineSegment(sketch, "E375", {"start": v(-7.48, 23.25) * mm, "end": v(-6.74, 24.6) * mm});
            skLineSegment(sketch, "E376", {"start": v(-6.74, 24.6) * mm, "end": v(-5.73, 25.93) * mm});
            skLineSegment(sketch, "E377", {"start": v(-5.73, 25.93) * mm, "end": v(-4.67, 26.68) * mm});
            skLineSegment(sketch, "E378", {"start": v(-4.67, 26.68) * mm, "end": v(-3.54, 27.29) * mm});
            skLineSegment(sketch, "E379", {"start": v(-3.54, 27.29) * mm, "end": v(-3.64, 28.5) * mm});
            skLineSegment(sketch, "E380", {"start": v(-3.64, 28.5) * mm, "end": v(-3.94, 29.75) * mm});
            skLineSegment(sketch, "E381", {"start": v(-3.94, 29.75) * mm, "end": v(-4.54, 30.8) * mm});
            skLineSegment(sketch, "E382", {"start": v(-4.54, 30.8) * mm, "end": v(-5.42, 31.98) * mm});
            skLineSegment(sketch, "E383", {"start": v(-5.42, 31.98) * mm, "end": v(-6.42, 33.06) * mm});
            skLineSegment(sketch, "E384", {"start": v(-6.42, 33.06) * mm, "end": v(-7.38, 33.73) * mm});
            skLineSegment(sketch, "E385", {"start": v(-7.38, 33.73) * mm, "end": v(-9.43, 34.39) * mm});
            skLineSegment(sketch, "E386", {"start": v(-9.43, 34.39) * mm, "end": v(-11.02, 34.39) * mm});
            skLineSegment(sketch, "E387", {"start": v(-11.02, 34.39) * mm, "end": v(-11.75, 34.24) * mm});
            skLineSegment(sketch, "E388", {"start": v(-11.75, 34.24) * mm, "end": v(-13.03, 33.69) * mm});
            skLineSegment(sketch, "E389", {"start": v(-13.03, 33.69) * mm, "end": v(-14.29, 32.81) * mm});
            skLineSegment(sketch, "E390", {"start": v(-14.29, 32.81) * mm, "end": v(-15.34, 31.87) * mm});
            skLineSegment(sketch, "E391", {"start": v(-15.34, 31.87) * mm, "end": v(-16.02, 30.94) * mm});
            skLineSegment(sketch, "E392", {"start": v(-16.02, 30.94) * mm, "end": v(-16.29, 30.2) * mm});
            skLineSegment(sketch, "E393", {"start": v(-16.29, 30.2) * mm, "end": v(-16.29, 28.83) * mm});
            skLineSegment(sketch, "E394", {"start": v(-16.29, 28.83) * mm, "end": v(-15.85, 28.18) * mm});
            skLineSegment(sketch, "E395", {"start": v(-15.85, 28.18) * mm, "end": v(-8.22, 22.23) * mm});
            skLineSegment(sketch, "E396", {"start": v(-8.22, 22.23) * mm, "end": v(-7.97, 22.23) * mm});
            skLineSegment(sketch, "E397.MirrorCS", {"start": v(-16.76, -15.53) * mm, "end": v(-16.35, -15.66) * mm});
            skLineSegment(sketch, "E398.MirrorCS", {"start": v(-16.84, -15.79) * mm, "end": v(-16.76, -15.53) * mm});
            skLineSegment(sketch, "E399.MirrorCS", {"start": v(11.62, -19.95) * mm, "end": v(11.36, -19.42) * mm});
            skLineSegment(sketch, "E400.MirrorCS", {"start": v(-1.87, -27.75) * mm, "end": v(-1.71, -27.27) * mm});
            skLineSegment(sketch, "E401.MirrorCS", {"start": v(6.07, -15.33) * mm, "end": v(6.75, -15.92) * mm});
            skLineSegment(sketch, "E402.MirrorCS", {"start": v(11.36, -19.42) * mm, "end": v(11.02, -19.32) * mm});
            skLineSegment(sketch, "E403.MirrorCS", {"start": v(6.75, -15.92) * mm, "end": v(7.44, -16.49) * mm});
            skLineSegment(sketch, "E404.MirrorCS", {"start": v(11.02, -19.32) * mm, "end": v(10.09, -19.43) * mm});
            skLineSegment(sketch, "E405.MirrorCS", {"start": v(-25.46, 6.94) * mm, "end": v(-24.3, 6.56) * mm});
            skLineSegment(sketch, "E406.MirrorCS", {"start": v(7.44, -16.49) * mm, "end": v(8.28, -17) * mm});
            skLineSegment(sketch, "E407.MirrorCS", {"start": v(-24.3, 6.56) * mm, "end": v(-24.17, 5.75) * mm});
            skLineSegment(sketch, "E408.MirrorCS", {"start": v(10.09, -19.43) * mm, "end": v(8.76, -19.37) * mm});
            skLineSegment(sketch, "E409.MirrorCS", {"start": v(8.28, -17) * mm, "end": v(8.9, -17.2) * mm});
            skLineSegment(sketch, "E410.MirrorCS", {"start": v(8.9, -17.2) * mm, "end": v(9.84, -17.5) * mm});
            skLineSegment(sketch, "E411.MirrorCS", {"start": v(-32.78, -8.74) * mm, "end": v(-32.28, -8.9) * mm});
            skLineSegment(sketch, "E412.MirrorCS", {"start": v(-32.08, -9.24) * mm, "end": v(-31.98, -9.45) * mm});
            skLineSegment(sketch, "E413.MirrorCS", {"start": v(-20.75, 0.96) * mm, "end": v(-20.79, 0.84) * mm});
            skLineSegment(sketch, "E414.MirrorCS", {"start": v(-2.38, -28.86) * mm, "end": v(-1.95, -28.33) * mm});
            skLineSegment(sketch, "E415.MirrorCS", {"start": v(-21.56, 1.68) * mm, "end": v(-20.75, 0.96) * mm});
            skLineSegment(sketch, "E416.MirrorCS", {"start": v(-1.95, -28.33) * mm, "end": v(-1.87, -27.75) * mm});
            skLineSegment(sketch, "E417.MirrorCS", {"start": v(11.91, -20.6) * mm, "end": v(11.62, -19.95) * mm});
            skLineSegment(sketch, "E418.MirrorCS", {"start": v(13.54, -16.76) * mm, "end": v(14.15, -16.31) * mm});
            skLineSegment(sketch, "E419.MirrorCS", {"start": v(12.49, -23.91) * mm, "end": v(12.43, -22.75) * mm});
            skLineSegment(sketch, "E420.MirrorCS", {"start": v(-29.3, -13.2) * mm, "end": v(-29.58, -11.44) * mm});
            skLineSegment(sketch, "E421.MirrorCS", {"start": v(-24.04, 15.16) * mm, "end": v(-24.86, 16.05) * mm});
            skLineSegment(sketch, "E422.MirrorCS", {"start": v(-26.9, 6.91) * mm, "end": v(-25.46, 6.94) * mm});
            skLineSegment(sketch, "E423.MirrorCS", {"start": v(-29.58, -11.44) * mm, "end": v(-29.56, -10.13) * mm});
            skLineSegment(sketch, "E424.MirrorCS", {"start": v(4.92, -30.1) * mm, "end": v(5.95, -30.24) * mm});
            skLineSegment(sketch, "E425.MirrorCS", {"start": v(-24.86, 16.05) * mm, "end": v(-25.7, 17.25) * mm});
            skLineSegment(sketch, "E426.MirrorCS", {"start": v(-29.56, -10.13) * mm, "end": v(-29.14, -8.83) * mm});
            skLineSegment(sketch, "E427.MirrorCS", {"start": v(-17.58, -7.77) * mm, "end": v(-18.05, -9.23) * mm});
            skLineSegment(sketch, "E428.MirrorCS", {"start": v(-18.05, -9.23) * mm, "end": v(-18.46, -10.48) * mm});
            skLineSegment(sketch, "E429.MirrorCS", {"start": v(9.84, -17.5) * mm, "end": v(10.7, -17.65) * mm});
            skLineSegment(sketch, "E430.MirrorCS", {"start": v(12.24, -17.37) * mm, "end": v(12.7, -17.13) * mm});
            skLineSegment(sketch, "E431.MirrorCS", {"start": v(10.7, -17.65) * mm, "end": v(11.32, -17.57) * mm});
            skLineSegment(sketch, "E432.MirrorCS", {"start": v(12.44, -24.66) * mm, "end": v(12.49, -23.91) * mm});
            skLineSegment(sketch, "E433.MirrorCS", {"start": v(-3.08, -29.4) * mm, "end": v(-2.38, -28.86) * mm});
            skLineSegment(sketch, "E434.MirrorCS", {"start": v(12.7, -17.13) * mm, "end": v(13.54, -16.76) * mm});
            skLineSegment(sketch, "E435.MirrorCS", {"start": v(11.32, -17.57) * mm, "end": v(12.24, -17.37) * mm});
            skLineSegment(sketch, "E436.MirrorCS", {"start": v(-32.4, 4.15) * mm, "end": v(-30.9, 5.5) * mm});
            skLineSegment(sketch, "E437.MirrorCS", {"start": v(-19.86, 15.67) * mm, "end": v(-20.9, 14.9) * mm});
            skLineSegment(sketch, "E438.MirrorCS", {"start": v(-20.64, 27.03) * mm, "end": v(-19.35, 26.6) * mm});
            skLineSegment(sketch, "E439.MirrorCS", {"start": v(1.75, -27.1) * mm, "end": v(1.83, -27.8) * mm});
            skLineSegment(sketch, "E440.MirrorCS", {"start": v(12.33, -21.96) * mm, "end": v(12.13, -21.24) * mm});
            skLineSegment(sketch, "E441.MirrorCS", {"start": v(7.92, -8.41) * mm, "end": v(7.56, -8.9) * mm});
            skLineSegment(sketch, "E442.MirrorCS", {"start": v(-5.05, -5.74) * mm, "end": v(-4.86, -5.23) * mm});
            skLineSegment(sketch, "E443.MirrorCS", {"start": v(-11.16, -19.05) * mm, "end": v(-11.95, -20.78) * mm});
            skLineSegment(sketch, "E444.MirrorCS", {"start": v(-12.8, -16.7) * mm, "end": v(-11.36, -17.26) * mm});
            skLineSegment(sketch, "E445.MirrorCS", {"start": v(-25.55, -17.18) * mm, "end": v(-26.35, -16.92) * mm});
            skLineSegment(sketch, "E446.MirrorCS", {"start": v(-10.23, 9.18) * mm, "end": v(-10.72, 10.83) * mm});
            skLineSegment(sketch, "E447.MirrorCS", {"start": v(-13.93, -16) * mm, "end": v(-12.8, -16.7) * mm});
            skLineSegment(sketch, "E448.MirrorCS", {"start": v(-9.65, -19.54) * mm, "end": v(-11.16, -19.05) * mm});
            skLineSegment(sketch, "E449.MirrorCS", {"start": v(-26.35, -16.92) * mm, "end": v(-26.97, -16.4) * mm});
            skLineSegment(sketch, "E450.MirrorCS", {"start": v(-4.86, -5.23) * mm, "end": v(-3.04, -3.39) * mm});
            skLineSegment(sketch, "E451.MirrorCS", {"start": v(8.18, -8.08) * mm, "end": v(7.92, -8.41) * mm});
            skLineSegment(sketch, "E452.MirrorCS", {"start": v(12.13, -21.24) * mm, "end": v(11.91, -20.6) * mm});
            skLineSegment(sketch, "E453.MirrorCS", {"start": v(-19.35, 26.6) * mm, "end": v(-18.87, 26) * mm});
            skLineSegment(sketch, "E454.MirrorCS", {"start": v(1.83, -27.8) * mm, "end": v(2.01, -28.4) * mm});
            skLineSegment(sketch, "E455.MirrorCS", {"start": v(-30.9, 5.5) * mm, "end": v(-29.3, 6.4) * mm});
            skLineSegment(sketch, "E456.MirrorCS", {"start": v(-20.9, 14.9) * mm, "end": v(-21.82, 14.02) * mm});
            skLineSegment(sketch, "E457.MirrorCS", {"start": v(-23.15, -17.44) * mm, "end": v(-25.55, -17.18) * mm});
            skLineSegment(sketch, "E458.MirrorCS", {"start": v(-14.88, -15.08) * mm, "end": v(-13.93, -16) * mm});
            skLineSegment(sketch, "E459.MirrorCS", {"start": v(-11.95, -20.78) * mm, "end": v(-12.29, -22.34) * mm});
            skLineSegment(sketch, "E460.MirrorCS", {"start": v(-21.43, 27.01) * mm, "end": v(-20.64, 27.03) * mm});
            skLineSegment(sketch, "E461.MirrorCS", {"start": v(-11.36, -17.26) * mm, "end": v(-10.1, -17.38) * mm});
            skLineSegment(sketch, "E462.MirrorCS", {"start": v(-9.7, 7.98) * mm, "end": v(-10.23, 9.18) * mm});
            skLineSegment(sketch, "E463.MirrorCS", {"start": v(-5.02, -6.83) * mm, "end": v(-5.05, -5.74) * mm});
            skLineSegment(sketch, "E464.MirrorCS", {"start": v(-33.01, 2.85) * mm, "end": v(-32.4, 4.15) * mm});
            skLineSegment(sketch, "E465.MirrorCS", {"start": v(-3.04, -3.39) * mm, "end": v(-4.95, -4.28) * mm});
            skLineSegment(sketch, "E466.MirrorCS", {"start": v(-26.97, -16.4) * mm, "end": v(-28.25, -15.08) * mm});
            skLineSegment(sketch, "E467.MirrorCS", {"start": v(-8.3, -19.35) * mm, "end": v(-9.65, -19.54) * mm});
            skLineSegment(sketch, "E468.MirrorCS", {"start": v(-18.28, 16.22) * mm, "end": v(-19.86, 15.67) * mm});
            skLineSegment(sketch, "E469.MirrorCS", {"start": v(2.01, -28.4) * mm, "end": v(2.37, -29.12) * mm});
            skLineSegment(sketch, "E470.MirrorCS", {"start": v(-21.82, 14.02) * mm, "end": v(-22.94, 14.49) * mm});
            skLineSegment(sketch, "E471.MirrorCS", {"start": v(12.43, -22.75) * mm, "end": v(12.33, -21.96) * mm});
            skLineSegment(sketch, "E472.MirrorCS", {"start": v(-29.3, 6.4) * mm, "end": v(-28.16, 6.8) * mm});
            skLineSegment(sketch, "E473.MirrorCS", {"start": v(-22.53, 26.65) * mm, "end": v(-21.43, 27.01) * mm});
            skLineSegment(sketch, "E474.MirrorCS", {"start": v(5.63, -14.85) * mm, "end": v(6.07, -15.33) * mm});
            skLineSegment(sketch, "E475.MirrorCS", {"start": v(-12.29, -22.34) * mm, "end": v(-12.36, -24.04) * mm});
            skLineSegment(sketch, "E476.MirrorCS", {"start": v(-10.1, -17.38) * mm, "end": v(-8.8, -17.2) * mm});
            skLineSegment(sketch, "E477.MirrorCS", {"start": v(-8.86, 6.51) * mm, "end": v(-9.7, 7.98) * mm});
            skLineSegment(sketch, "E478.MirrorCS", {"start": v(-33.4, 0.68) * mm, "end": v(-33.01, 2.85) * mm});
            skLineSegment(sketch, "E479.MirrorCS", {"start": v(-28.25, -15.08) * mm, "end": v(-29.3, -13.2) * mm});
            skLineSegment(sketch, "E480.MirrorCS", {"start": v(-16.77, 16.5) * mm, "end": v(-18.28, 16.22) * mm});
            skLineSegment(sketch, "E481.MirrorCS", {"start": v(-6.31, -18.6) * mm, "end": v(-8.3, -19.35) * mm});
            skLineSegment(sketch, "E482.MirrorCS", {"start": v(-13.61, 5.88) * mm, "end": v(-12.58, 6.89) * mm});
            skLineSegment(sketch, "E483.MirrorCS", {"start": v(2.37, -29.12) * mm, "end": v(3.11, -29.51) * mm});
            skLineSegment(sketch, "E484.MirrorCS", {"start": v(-15.56, 16.9) * mm, "end": v(-15.64, 16.66) * mm});
            skLineSegment(sketch, "E485.MirrorCS", {"start": v(-28.16, 6.8) * mm, "end": v(-26.9, 6.91) * mm});
            skLineSegment(sketch, "E486.MirrorCS", {"start": v(-22.94, 14.49) * mm, "end": v(-24.04, 15.16) * mm});
            skLineSegment(sketch, "E487.MirrorCS", {"start": v(-20.5, -17) * mm, "end": v(-23.15, -17.44) * mm});
            skLineSegment(sketch, "E488.MirrorCS", {"start": v(-15.47, -14.13) * mm, "end": v(-14.88, -15.08) * mm});
            skLineSegment(sketch, "E489.MirrorCS", {"start": v(-12.36, -24.04) * mm, "end": v(-11.97, -26.14) * mm});
            skLineSegment(sketch, "E490.MirrorCS", {"start": v(-8.8, -17.2) * mm, "end": v(-7.85, -16.77) * mm});
            skLineSegment(sketch, "E491.MirrorCS", {"start": v(-12.58, 6.89) * mm, "end": v(-12.85, 8.33) * mm});
            skLineSegment(sketch, "E492.MirrorCS", {"start": v(3.11, -29.51) * mm, "end": v(4.92, -30.1) * mm});
            skLineSegment(sketch, "E493.MirrorCS", {"start": v(-4.96, -4.06) * mm, "end": v(-4.69, -2.28) * mm});
            skLineSegment(sketch, "E494.MirrorCS", {"start": v(-11.97, -26.14) * mm, "end": v(-11.32, -27.57) * mm});
            skLineSegment(sketch, "E495.MirrorCS", {"start": v(-7.85, -16.77) * mm, "end": v(-6.3, -15.84) * mm});
            skLineSegment(sketch, "E496.MirrorCS", {"start": v(-4.69, -2.28) * mm, "end": v(-5.98, -4.67) * mm});
            skLineSegment(sketch, "E497.MirrorCS", {"start": v(5.95, -30.24) * mm, "end": v(7.04, -30.24) * mm});
            skLineSegment(sketch, "E498.MirrorCS", {"start": v(-6.3, -15.84) * mm, "end": v(-5.12, -14.81) * mm});
            skLineSegment(sketch, "E499.MirrorCS", {"start": v(-11.32, -27.57) * mm, "end": v(-10.23, -28.9) * mm});
            skLineSegment(sketch, "E500.MirrorCS", {"start": v(-5.98, -4.67) * mm, "end": v(-7.13, -5) * mm});
            skLineSegment(sketch, "E501.MirrorCS", {"start": v(-25.7, 17.25) * mm, "end": v(-26.42, 18.54) * mm});
            skLineSegment(sketch, "E502.MirrorCS", {"start": v(-29.14, -8.83) * mm, "end": v(-28.42, -8.25) * mm});
            skLineSegment(sketch, "E503.MirrorCS", {"start": v(7.04, -30.24) * mm, "end": v(8.25, -30.01) * mm});
            skLineSegment(sketch, "E504.MirrorCS", {"start": v(-10.23, -28.9) * mm, "end": v(-8.2, -29.86) * mm});
            skLineSegment(sketch, "E505.MirrorCS", {"start": v(-24.17, 5.75) * mm, "end": v(-23.75, 4.58) * mm});
            skLineSegment(sketch, "E506.MirrorCS", {"start": v(8.76, -19.37) * mm, "end": v(7.01, -18.8) * mm});
            skLineSegment(sketch, "E507.MirrorCS", {"start": v(-26.42, 18.54) * mm, "end": v(-26.76, 19.66) * mm});
            skLineSegment(sketch, "E508.MirrorCS", {"start": v(8.25, -30.01) * mm, "end": v(9.3, -29.69) * mm});
            skLineSegment(sketch, "E509.MirrorCS", {"start": v(-6.99, -9.26) * mm, "end": v(-7.67, -8.1) * mm});
            skLineSegment(sketch, "E510.MirrorCS", {"start": v(-8.2, -29.86) * mm, "end": v(-6.07, -30.15) * mm});
            skLineSegment(sketch, "E511.MirrorCS", {"start": v(-23.75, 4.58) * mm, "end": v(-23.3, 3.68) * mm});
            skLineSegment(sketch, "E512.MirrorCS", {"start": v(-28.66, -4.46) * mm, "end": v(-29.93, -4.77) * mm});
            skLineSegment(sketch, "E513.MirrorCS", {"start": v(7.01, -18.8) * mm, "end": v(5.92, -18.44) * mm});
            skLineSegment(sketch, "E514.MirrorCS", {"start": v(-26.76, 19.66) * mm, "end": v(-26.75, 21.8) * mm});
            skLineSegment(sketch, "E515.MirrorCS", {"start": v(-28.42, -8.25) * mm, "end": v(-27.58, -7.96) * mm});
            skLineSegment(sketch, "E516.MirrorCS", {"start": v(-17.99, -13.1) * mm, "end": v(-17.52, -14.61) * mm});
            skLineSegment(sketch, "E517.MirrorCS", {"start": v(-26.75, 21.8) * mm, "end": v(-26.26, 23.32) * mm});
            skLineSegment(sketch, "E518.MirrorCS", {"start": v(9.3, -29.69) * mm, "end": v(10.38, -28.94) * mm});
            skLineSegment(sketch, "E519.MirrorCS", {"start": v(3.63, -3.57) * mm, "end": v(5.57, -5.8) * mm});
            skLineSegment(sketch, "E520.MirrorCS", {"start": v(-16.01, -10.56) * mm, "end": v(-16.17, -11.6) * mm});
            skLineSegment(sketch, "E521.MirrorCS", {"start": v(-24.97, 25.01) * mm, "end": v(-23.75, 25.94) * mm});
            skLineSegment(sketch, "E522.MirrorCS", {"start": v(-8.05, 5.46) * mm, "end": v(-6.1, 5.8) * mm});
            skLineSegment(sketch, "E523.MirrorCS", {"start": v(-23.75, 25.94) * mm, "end": v(-22.53, 26.65) * mm});
            skLineSegment(sketch, "E524.MirrorCS", {"start": v(-6.07, -30.15) * mm, "end": v(-4.17, -29.77) * mm});
            skLineSegment(sketch, "E525.MirrorCS", {"start": v(-23.3, 3.68) * mm, "end": v(-22.76, 2.7) * mm});
            skLineSegment(sketch, "E526.MirrorCS", {"start": v(-7.67, -8.1) * mm, "end": v(-8.65, -7.8) * mm});
            skLineSegment(sketch, "E527.MirrorCS", {"start": v(-6.1, 5.8) * mm, "end": v(-8.86, 6.51) * mm});
            skLineSegment(sketch, "E528.MirrorCS", {"start": v(-10.89, 4.63) * mm, "end": v(-9.15, 5.1) * mm});
            skLineSegment(sketch, "E529.MirrorCS", {"start": v(-29.93, -4.77) * mm, "end": v(-30.7, -4.51) * mm});
            skLineSegment(sketch, "E530.MirrorCS", {"start": v(-26.26, 23.32) * mm, "end": v(-25.9, 23.97) * mm});
            skLineSegment(sketch, "E531.MirrorCS", {"start": v(-33, -1.2) * mm, "end": v(-33.4, 0.68) * mm});
            skLineSegment(sketch, "E532.MirrorCS", {"start": v(-32.45, -2.46) * mm, "end": v(-33, -1.2) * mm});
            skLineSegment(sketch, "E533.MirrorCS", {"start": v(5.2, -17.84) * mm, "end": v(4.67, -17.6) * mm});
            skLineSegment(sketch, "E534.MirrorCS", {"start": v(-25.9, 23.97) * mm, "end": v(-24.97, 25.01) * mm});
            skLineSegment(sketch, "E535.MirrorCS", {"start": v(5.5, -4.4) * mm, "end": v(3.63, -3.57) * mm});
            skLineSegment(sketch, "E536.MirrorCS", {"start": v(-4.17, -29.77) * mm, "end": v(-3.08, -29.4) * mm});
            skLineSegment(sketch, "E537.MirrorCS", {"start": v(-15.64, 16.66) * mm, "end": v(-16.77, 16.5) * mm});
            skLineSegment(sketch, "E538.MirrorCS", {"start": v(-14.01, -7.57) * mm, "end": v(-15.08, -7.7) * mm});
            skLineSegment(sketch, "E539.MirrorCS", {"start": v(-6.72, 4) * mm, "end": v(-8.05, 5.46) * mm});
            skLineSegment(sketch, "E540.MirrorCS", {"start": v(10.38, -28.94) * mm, "end": v(11.11, -28.17) * mm});
            skLineSegment(sketch, "E541.MirrorCS", {"start": v(-8.65, -7.8) * mm, "end": v(-11.57, -7.49) * mm});
            skLineSegment(sketch, "E542.MirrorCS", {"start": v(11.5, -27.52) * mm, "end": v(12.44, -24.66) * mm});
            skLineSegment(sketch, "E543.MirrorCS", {"start": v(-4.53, -17.55) * mm, "end": v(-6.31, -18.6) * mm});
            skLineSegment(sketch, "E544.MirrorCS", {"start": v(-22.76, 2.7) * mm, "end": v(-21.56, 1.68) * mm});
            skLineSegment(sketch, "E545.MirrorCS", {"start": v(5.92, -18.44) * mm, "end": v(5.2, -17.84) * mm});
            skLineSegment(sketch, "E546.MirrorCS", {"start": v(-31.44, -3.9) * mm, "end": v(-32.45, -2.46) * mm});
            skLineSegment(sketch, "E547.MirrorCS", {"start": v(-15.96, -12.84) * mm, "end": v(-15.47, -14.13) * mm});
            skLineSegment(sketch, "E548.MirrorCS", {"start": v(11.11, -28.17) * mm, "end": v(11.5, -27.52) * mm});
            skLineSegment(sketch, "E549.MirrorCS", {"start": v(-17.52, -14.61) * mm, "end": v(-18.58, -15.73) * mm});
            skLineSegment(sketch, "E550.MirrorCS", {"start": v(-18.58, -15.73) * mm, "end": v(-20.5, -17) * mm});
            skLineSegment(sketch, "E551.MirrorCS", {"start": v(-15.08, -7.7) * mm, "end": v(-16.01, -10.56) * mm});
            skLineSegment(sketch, "E552.MirrorCS", {"start": v(-16.17, -11.6) * mm, "end": v(-15.96, -12.84) * mm});
            skLineSegment(sketch, "E553.MirrorCS", {"start": v(-30.7, -4.51) * mm, "end": v(-31.44, -3.9) * mm});
            skLineSegment(sketch, "E554.MirrorCS", {"start": v(-18.46, -10.48) * mm, "end": v(-17.99, -13.1) * mm});
            skLineSegment(sketch, "E555.MirrorCS", {"start": v(-11.57, -7.49) * mm, "end": v(-14.01, -7.57) * mm});
            skLineSegment(sketch, "E556.MirrorCS", {"start": v(-9.15, 5.1) * mm, "end": v(-6.72, 4) * mm});
            skLineSegment(sketch, "E557.MirrorCS", {"start": v(-10.72, 10.83) * mm, "end": v(-14.62, 23.32) * mm});
            skLineSegment(sketch, "E558.MirrorCS", {"start": v(7.56, -8.9) * mm, "end": v(5.63, -14.85) * mm});
            skLineSegment(sketch, "E559.MirrorCS", {"start": v(-18.46, 2.54) * mm, "end": v(-13.61, 5.88) * mm});
            skLineSegment(sketch, "E560.MirrorCS", {"start": v(-1.71, -27.27) * mm, "end": v(-4.53, -17.55) * mm});
            skLineSegment(sketch, "E561.MirrorCS", {"start": v(-18.87, 26) * mm, "end": v(-15.56, 16.9) * mm});
            skLineSegment(sketch, "E562.MirrorCS", {"start": v(4.67, -17.6) * mm, "end": v(1.75, -27.1) * mm});
            skLineSegment(sketch, "E563.MirrorCS", {"start": v(0.16, -22.44) * mm, "end": v(-5.02, -6.83) * mm});
            skLineSegment(sketch, "E564.MirrorCS", {"start": v(-12.85, 8.33) * mm, "end": v(-14.53, 13.99) * mm});
            skArc(sketch, "E565.MirrorCS", {"start": v(-18.46, 2.54) * mm, "mid": v(-22.3, 10.26) * mm, "end": v(-14.53, 13.99) * mm});
            skLineSegment(sketch, "E566.MirrorCS", {"start": v(-5.12, -14.81) * mm, "end": v(-6.99, -9.26) * mm});
            skLineSegment(sketch, "E567.MirrorCS", {"start": v(-20.79, 0.84) * mm, "end": v(-28.66, -4.46) * mm});
            skLineSegment(sketch, "E568.MirrorCS", {"start": v(-7.13, -5) * mm, "end": v(-24.02, -4.96) * mm});
            skLineSegment(sketch, "E569.MirrorCS", {"start": v(-24.02, -4.96) * mm, "end": v(-10.89, 4.63) * mm});
            skLineSegment(sketch, "E570.MirrorCS", {"start": v(-27.58, -7.96) * mm, "end": v(-17.58, -7.77) * mm});
            skLineSegment(sketch, "E571.MirrorCS", {"start": v(5.57, -5.8) * mm, "end": v(0.16, -22.44) * mm});
            skLineSegment(sketch, "E572.MirrorCS", {"start": v(-4.95, -4.28) * mm, "end": v(-4.96, -4.06) * mm});
            skSolve(sketch);
        }
        {
            var Q0;
            Q0 = qSketchRegion(id + "F8", true);
            extrude(context, id + "F9", {"entities" : qUnion([Q0]), "operationType" : NewBodyOperationType.REMOVE, "oppositeDirection" : true, "depth" : 0.76 * mm});
        }
    });
